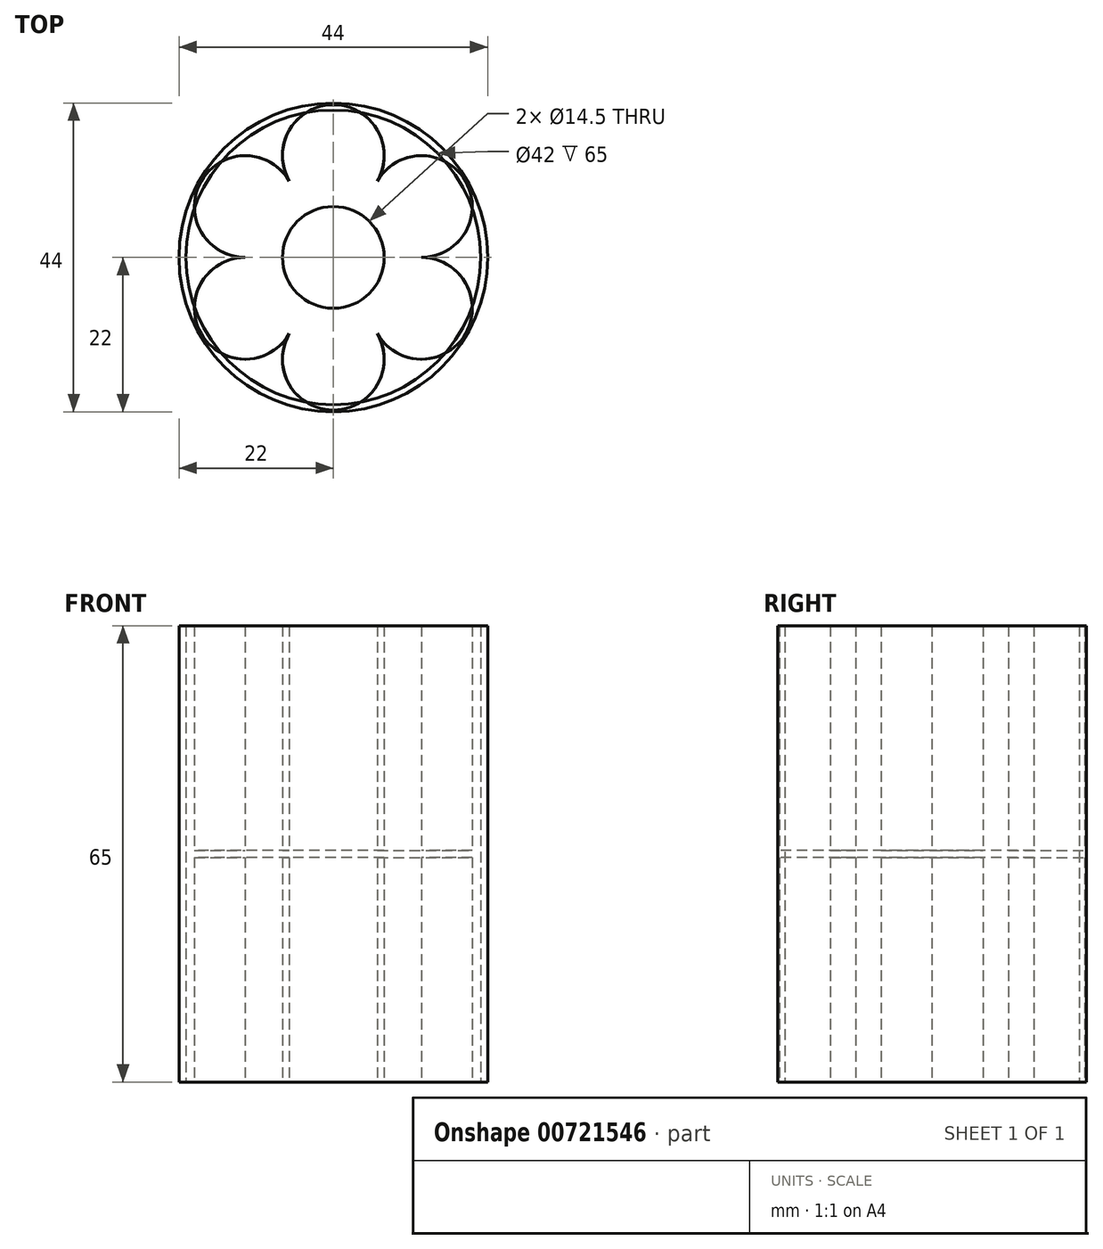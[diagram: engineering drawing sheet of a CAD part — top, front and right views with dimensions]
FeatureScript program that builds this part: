
annotation { "Feature Type Name" : "Feature", "Feature Type Description" : "" }
export const myFeature = defineFeature(function(context is Context, id is Id, definition is map)
    precondition{}
    {
        {
            var Q0;
            Q0=qCreatedBy(makeId("Top.planeOp"),FACE);
            var sketch = newSketch(context, id + "F0", { "sketchPlane" : qUnion([Q0])});
            skCircle(sketch, "E0", {"center": v(0, 14.5) * mm, "radius": 7.25 * mm});
            skCircle(sketch, "E1.1.0", {"center": v(-12.56, 7.25) * mm, "radius": 7.25 * mm});
            skPoint(sketch, "E1.center", {"position": v(0, 0) * mm});
            skCircle(sketch, "E2", {"center": v(0, 0) * mm, "radius": 21 * mm, "construction": true});
            skCircle(sketch, "E3.1.2.0", {"center": v(-12.56, -7.25) * mm, "radius": 7.25 * mm});
            skCircle(sketch, "E3.1.3.0", {"center": v(0, -14.5) * mm, "radius": 7.25 * mm});
            skCircle(sketch, "E4.1.4.0", {"center": v(12.56, -7.25) * mm, "radius": 7.25 * mm});
            skCircle(sketch, "E5", {"center": v(0, 0) * mm, "radius": 7.25 * mm});
            skCircle(sketch, "E6.1.5.0", {"center": v(12.56, 7.25) * mm, "radius": 7.25 * mm});
            skSolve(sketch);
        }
        {
            var Q0;
            Q0 = qSketchRegion(id + "F0", true);
            extrude(context, id + "F1", {"entities" : qUnion([Q0]), "depth" : 32 * mm, "offsetDistance" : 25 * mm});
        }
        {
            var Q0;
            Q0=makeQuery(id+"F1.opExtrude","CAP_FACE",FACE,{"disambiguationData":[OSD([sQuery(id+"F0.wireOp",EDGE,"E0")])],"isStart":false});
            var Q1;
            Q1=makeQuery(id+"F1.opExtrude","CAP_FACE",FACE,{"disambiguationData":[OSD([sQuery(id+"F0.wireOp",EDGE,"E1.1.0")])],"isStart":false});
            var Q2;
            Q2=makeQuery(id+"F1.opExtrude","CAP_FACE",FACE,{"disambiguationData":[OSD([sQuery(id+"F0.wireOp",EDGE,"E3.1.3.0")])],"isStart":false});
            var Q3;
            Q3=makeQuery(id+"F1.opExtrude","CAP_FACE",FACE,{"disambiguationData":[OSD([sQuery(id+"F0.wireOp",EDGE,"E3.1.2.0")])],"isStart":false});
            extrude(context, id + "F2", {"entities" : qUnion([Q0, Q1, Q2, Q3]), "depth" : 33 * mm, "offsetDistance" : 25 * mm, "hasSecondDirection" : true, "secondDirectionOppositeDirection" : true, "secondDirectionDepth" : -1 * mm});
        }
        {
            var Q0;
            Q0=qCreatedBy(makeId("Top.planeOp"),FACE);
            var sketch = newSketch(context, id + "F3", { "sketchPlane" : qUnion([Q0])});
            skCircle(sketch, "E7", {"center": v(0, 0) * mm, "radius": 21 * mm});
            skCircle(sketch, "E8", {"center": v(0, 0) * mm, "radius": 22 * mm});
            skSolve(sketch);
        }
        {
            var Q0;
            Q0 = qSketchRegion(id + "F3", true);
            extrude(context, id + "F4", {"entities" : qUnion([Q0]), "depth" : 65 * mm, "offsetDistance" : 25 * mm});
        }
    });
